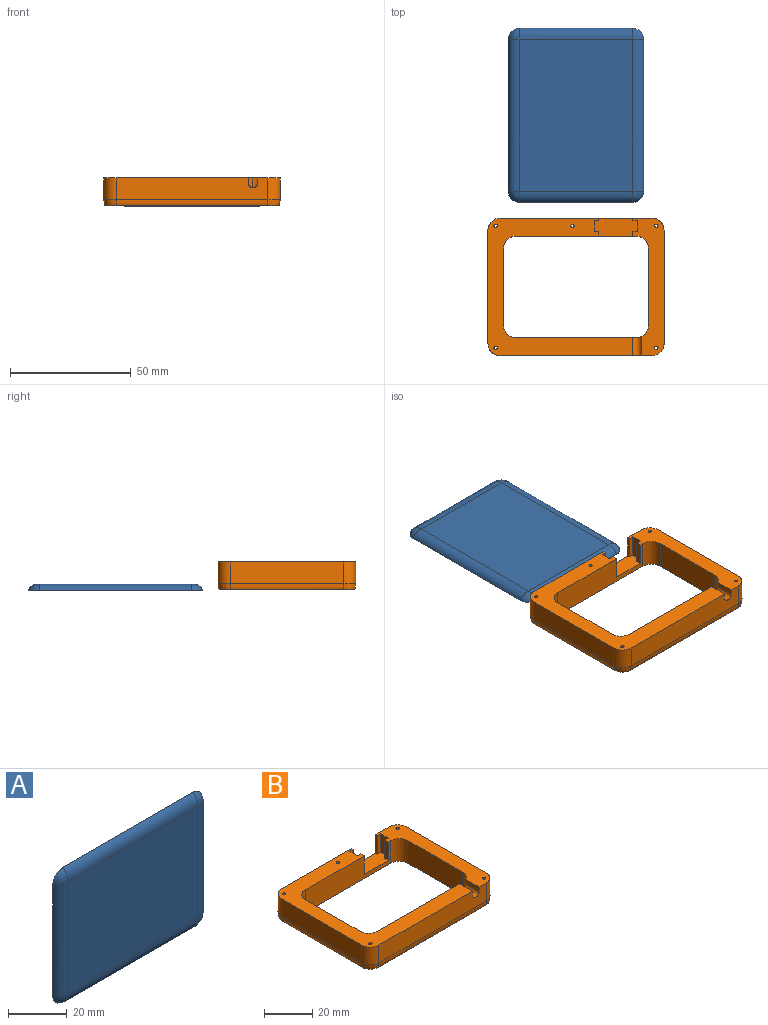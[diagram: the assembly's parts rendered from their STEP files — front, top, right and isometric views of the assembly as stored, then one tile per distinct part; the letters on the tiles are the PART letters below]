
ASSEMBLY  parts=2 mates=1
PART A: 20 faces, bbox 72.5x3x56.5 mm
  f0: plane 72.15x56.15mm, normal (0,1,0), area 4024.5mm2, adj f2,f4,f6,f8,f10,f11,f12,f13
  f1: plane 1.4x1.4mm, normal (0,1,0), area 1.5mm2, adj f2
  f2: cylinder r=0.7mm len=1.4mm, axis (0,1,0), area 2.2mm2, adj f0,f1
  f3: plane 1.4x1.4mm, normal (0,1,0), area 1.5mm2, adj f4
  f4: cylinder r=0.7mm len=1.4mm, axis (0,1,0), area 2.2mm2, adj f0,f3
  f5: plane 1.4x1.4mm, normal (0,1,0), area 1.5mm2, adj f6
  f6: cylinder r=0.7mm len=1.4mm, axis (0,1,0), area 2.2mm2, adj f0,f5
  f7: plane 1.4x1.4mm, normal (0,1,0), area 1.5mm2, adj f8
  f8: cylinder r=0.7mm len=1.4mm, axis (0,1,0), area 2.2mm2, adj f0,f7
  f9: plane 1.4x1.4mm, normal (0,1,0), area 1.5mm2, adj f10
  f10: cylinder r=0.7mm len=1.4mm, axis (0,1,0), area 2.2mm2, adj f0,f9
  f11: extruded ~63x4.57mm, area 350.5mm2, adj f0,f14,f17,f19
  f12: extruded ~47x4.57mm, area 261.5mm2, adj f0,f13,f14,f19
  f13: bspline ~4.75x4.75mm, area 22.4mm2, adj f0,f12,f15
  f14: bspline ~4.75x4.75mm, area 22.4mm2, adj f0,f11,f12
  f15: extruded ~63x4.57mm, area 350.5mm2, adj f0,f13,f16,f19
  f16: bspline ~4.75x4.75mm, area 22.4mm2, adj f0,f15,f18
  f17: bspline ~4.75x4.75mm, area 22.4mm2, adj f0,f11,f18
  f18: extruded ~47x4.57mm, area 261.5mm2, adj f0,f16,f17,f19
  f19: plane 63x47mm, normal (0,-1,0), area 2961mm2, adj f11,f12,f15,f18
PART B: 47 faces, bbox 73x57x11.7 mm
  f0: plane 72.15x56.15mm, normal (0,0,-1), area 1526mm2, adj f12,f13,f14,f17,f18,f19,f22,f23
  f1: plane 9.3x2mm, normal (0,1,0), area 18.6mm2, adj f2,f15,f16,f21
  f2: plane 9.3x4.5mm, normal (-1,0,0), area 41.8mm2, adj f1,f3,f16,f21
  f3: plane 9.3x2mm, normal (0,-1,0), area 18.6mm2, adj f2,f8,f16,f21
  f4: plane 9.3x2mm, normal (0,-1,0), area 18.6mm2, adj f5,f21,f25,f30
  f5: plane 9.3x4.5mm, normal (1,0,0), area 41.8mm2, adj f4,f6,f21,f25
  f6: plane 9.3x2mm, normal (0,1,0), area 18.6mm2, adj f5,f20,f21,f25
  f7: plane 9x8mm, normal (0,1,0), area 72mm2, adj f8,f16,f35,f40
  f8: plane 9.3x1mm, normal (-1,0,0), area 9.3mm2, adj f3,f7,f16,f21,f40
  f9: plane 7.5x2mm, normal (1,0,0), area 15mm2, adj f11,f12,f25,f36
  f10: plane 8.04x2mm, normal (-1,0,0), area 16.1mm2, adj f11,f13,f16,f36
  f11: cylinder r=2mm len=8.04mm, axis (0,-1,0), area 48mm2, adj f9,f10,f12,f13,f36
  f12: plane 50x11.5mm, normal (0,1,0), area 568.9mm2, adj f0,f9,f11,f13,f24,f25
  f13: cylinder r=5mm len=11.5mm, axis (0,0,1), area 83.3mm2, adj f0,f10,f11,f12,f14,f16
  f14: plane 32x11.5mm, normal (-1,0,0), area 368mm2, adj f0,f13,f16,f19
  f15: plane 9.3x2mm, normal (-1,0,0), area 18.6mm2, adj f1,f16,f21,f22
  f16: plane 57x13mm, normal (0,0,1), area 427.4mm2, adj f1,f2,f3,f7,f8,f10,f13,f14
  f17: cylinder r=0.7mm len=11.5mm, axis (0,0,1), area 50.6mm2, adj f0,f16
  f18: cylinder r=0.7mm len=11.5mm, axis (0,0,1), area 50.6mm2, adj f0,f16
  f19: cylinder r=5mm len=11.5mm, axis (0,0,1), area 90.3mm2, adj f0,f14,f16,f22
  f20: plane 9.3x2mm, normal (1,0,0), area 18.6mm2, adj f6,f21,f22,f25
  f21: plane 18x7.5mm, normal (0,0,1), area 122.9mm2, adj f1,f2,f3,f4,f5,f6,f8,f15
  f22: plane 50x11.5mm, normal (0,-1,0), area 444.8mm2, adj f0,f15,f16,f19,f20,f21,f23,f25
  f23: cylinder r=5mm len=11.5mm, axis (0,0,1), area 90.3mm2, adj f0,f22,f25,f29
  f24: cylinder r=5mm len=11.5mm, axis (0,0,1), area 90.3mm2, adj f0,f12,f25,f29
  f25: plane 59.75x57mm, normal (0,0,1), area 1052.5mm2, adj f4,f5,f6,f9,f12,f20,f22,f23
  f26: cylinder r=0.7mm len=11.5mm, axis (0,0,1), area 50.6mm2, adj f0,f25
  f27: cylinder r=0.7mm len=11.5mm, axis (0,0,1), area 50.6mm2, adj f0,f25
  f28: cylinder r=0.7mm len=11.5mm, axis (0,0,1), area 50.6mm2, adj f0,f25
  f29: plane 32x11.5mm, normal (1,0,0), area 368mm2, adj f0,f23,f24,f25
  f30: plane 9.3x1mm, normal (1,0,0), area 9.3mm2, adj f4,f21,f25,f31,f40
  f31: plane 41x9mm, normal (0,1,0), area 369mm2, adj f25,f30,f40,f41
  f32: plane 47x9mm, normal (1,0,0), area 423mm2, adj f16,f33,f34,f35
  f33: cylinder r=5mm len=9mm, axis (0,0,1), area 70.7mm2, adj f16,f32,f36,f37
  f34: extruded ~47x2.5mm, area 120mm2, adj f0,f32,f37,f46
  f35: cylinder r=5mm len=9mm, axis (0,0,1), area 70.7mm2, adj f7,f16,f32,f46
  f36: plane 63x9mm, normal (0,-1,0), area 552.7mm2, adj f9,f10,f11,f16,f25,f33,f38,f39
  f37: bspline ~5x5mm, area 19.5mm2, adj f0,f33,f34,f39
  f38: cylinder r=5mm len=9mm, axis (0,0,1), area 70.7mm2, adj f25,f36,f43,f44
  f39: extruded ~63x2.5mm, area 160.8mm2, adj f0,f36,f37,f44
  f40: extruded ~63x2.5mm, area 156.6mm2, adj f0,f7,f8,f21,f30,f31,f42,f46
  f41: cylinder r=5mm len=9mm, axis (0,0,1), area 70.7mm2, adj f25,f31,f42,f43
  f42: bspline ~5x5mm, area 19.5mm2, adj f0,f40,f41,f45
  f43: plane 47x9mm, normal (-1,0,0), area 423mm2, adj f25,f38,f41,f45
  f44: bspline ~5x5mm, area 19.5mm2, adj f0,f38,f39,f45
  f45: extruded ~47x2.5mm, area 120mm2, adj f0,f42,f43,f44
  f46: bspline ~5x5mm, area 19.5mm2, adj f0,f34,f35,f40
PLACE A rot(axis=(-0.58,0.58,-0.58),120deg) t=(15.82,52.1,-7.48)mm
PLACE B t=(15.83,14.6,4.19)mm
MATE parallel A.f0 <-> B.f0  axis (0,0,-1) through (15.83,52.1,4.02)mm
